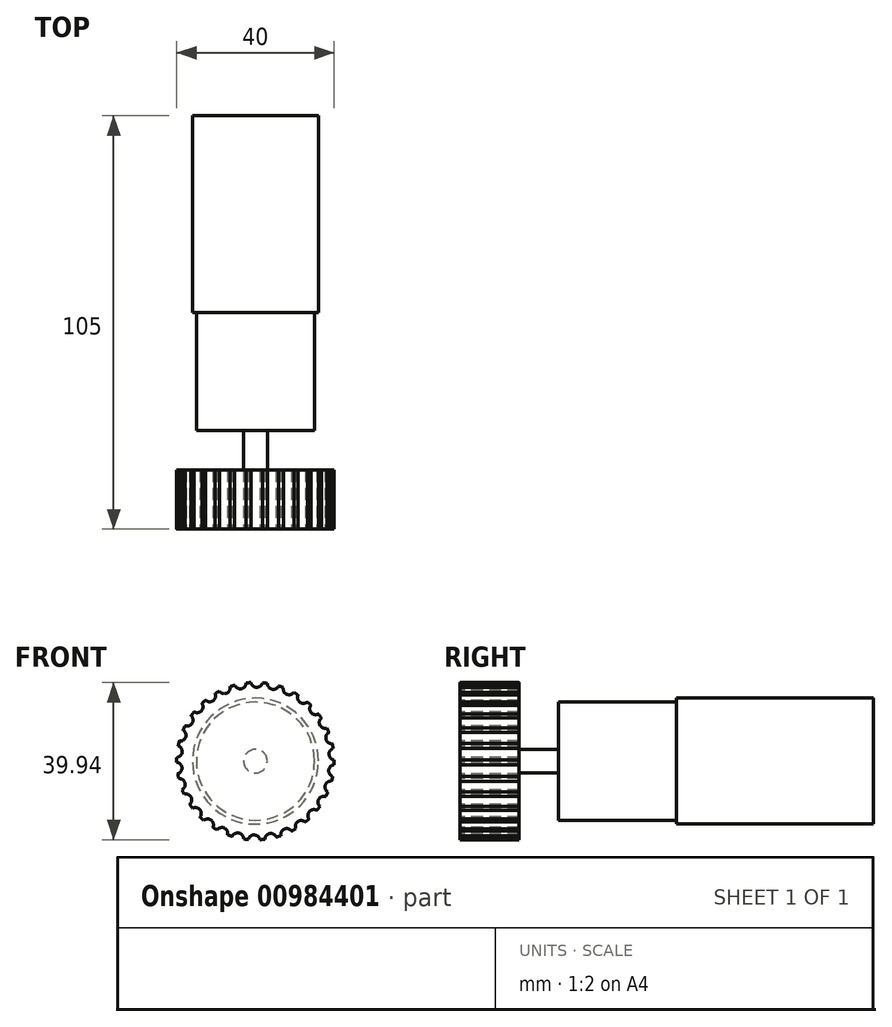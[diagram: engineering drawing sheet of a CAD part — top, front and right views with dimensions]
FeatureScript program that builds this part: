
annotation { "Feature Type Name" : "Feature", "Feature Type Description" : "" }
export const myFeature = defineFeature(function(context is Context, id is Id, definition is map)
    precondition{}
    {
        {
            var Q0;
            Q0=qCreatedBy(makeId("Front.planeOp"),FACE);
            var sketch = newSketch(context, id + "F0", { "sketchPlane" : qUnion([Q0])});
            skCircle(sketch, "E0", {"center": v(0, 0) * mm, "radius": 20 * mm});
            skCircle(sketch, "E1", {"center": v(0, 0) * mm, "radius": 3 * mm});
            skSolve(sketch);
        }
        {
            var Q0;
            Q0=makeQuery(id+"F0.imprint","IMPRINT",FACE,{"disambiguationData":[TD([[makeQuery(id+"F0.imprint","IMPRINT",EDGE,{"derivedFrom":sQuery(id+"F0.wireOp",EDGE,"E0")}),1.0]])]});
            extrude(context, id + "F1", {"entities" : qUnion([Q0]), "depth" : 15 * mm, "offsetDistance" : 25 * mm});
        }
        {
            var Q0;
            Q0=makeQuery(id+"F1.opExtrude","CAP_FACE",FACE,{"disambiguationData":[OSD([sQuery(id+"F0.wireOp",EDGE,"E0"),sQuery(id+"F0.wireOp",EDGE,"E1")])],"isStart":false});
            var sketch = newSketch(context, id + "F2", { "sketchPlane" : qUnion([Q0])});
            skCircle(sketch, "E2", {"center": v(20.17, 1.78) * mm, "radius": 1.5 * mm});
            skSolve(sketch);
        }
        {
            var Q0;
            Q0 = qSketchRegion(id + "F2", true);
            var Q1;
            Q1=sQuery(id+"F2.wireOp",EDGE,"E2");
            var Q2;
            Q2=makeQuery(id+"F1.opExtrude","CAP_FACE",FACE,{"disambiguationData":[OSD([sQuery(id+"F0.wireOp",EDGE,"E0"),sQuery(id+"F0.wireOp",EDGE,"E1")])],"isStart":true});
            extrude(context, id + "F3", {"entities" : qUnion([Q0]), "surfaceEntities" : qUnion([Q1]), "endBound" : BoundingType.UP_TO_SURFACE, "oppositeDirection" : true, "depth" : 25 * mm, "endBoundEntityFace" : qUnion([Q2]), "offsetDistance" : 25 * mm});
        }
        {
            var Q0;
            Q0=makeQuery(id+"F3.opExtrude","SWEPT_BODY",BODY,{"disambiguationData":[OSD([sQuery(id+"F2.wireOp",EDGE,"E2")])]});
            var Q1;
            Q1=makeQuery(id+"F1.opExtrude","SWEPT_FACE",FACE,{"disambiguationData":[OSD([sQuery(id+"F0.wireOp",EDGE,"E1")])]});
            circularPattern(context, id + "F4", {"entities" : qUnion([Q0]), "axis" : qUnion([Q1]), "angle" : 360 * degree, "instanceCount" : 30, "equalSpace" : true});
        }
        {
            var Q0;
            Q0=makeQuery(id+"F4.opPattern","COPY",BODY,{"derivedFrom":makeQuery(id+"F3.opExtrude","SWEPT_BODY",BODY,{"disambiguationData":[OSD([sQuery(id+"F2.wireOp",EDGE,"E2")])]}),"instanceName":"15"});
            var Q1;
            Q1=makeQuery(id+"F4.opPattern","COPY",BODY,{"derivedFrom":makeQuery(id+"F3.opExtrude","SWEPT_BODY",BODY,{"disambiguationData":[OSD([sQuery(id+"F2.wireOp",EDGE,"E2")])]}),"instanceName":"16"});
            var Q2;
            Q2=makeQuery(id+"F4.opPattern","COPY",BODY,{"derivedFrom":makeQuery(id+"F3.opExtrude","SWEPT_BODY",BODY,{"disambiguationData":[OSD([sQuery(id+"F2.wireOp",EDGE,"E2")])]}),"instanceName":"17"});
            var Q3;
            Q3=makeQuery(id+"F4.opPattern","COPY",BODY,{"derivedFrom":makeQuery(id+"F3.opExtrude","SWEPT_BODY",BODY,{"disambiguationData":[OSD([sQuery(id+"F2.wireOp",EDGE,"E2")])]}),"instanceName":"18"});
            var Q4;
            Q4=makeQuery(id+"F4.opPattern","COPY",BODY,{"derivedFrom":makeQuery(id+"F3.opExtrude","SWEPT_BODY",BODY,{"disambiguationData":[OSD([sQuery(id+"F2.wireOp",EDGE,"E2")])]}),"instanceName":"19"});
            var Q5;
            Q5=makeQuery(id+"F4.opPattern","COPY",BODY,{"derivedFrom":makeQuery(id+"F3.opExtrude","SWEPT_BODY",BODY,{"disambiguationData":[OSD([sQuery(id+"F2.wireOp",EDGE,"E2")])]}),"instanceName":"20"});
            var Q6;
            Q6=makeQuery(id+"F4.opPattern","COPY",BODY,{"derivedFrom":makeQuery(id+"F3.opExtrude","SWEPT_BODY",BODY,{"disambiguationData":[OSD([sQuery(id+"F2.wireOp",EDGE,"E2")])]}),"instanceName":"21"});
            var Q7;
            Q7=makeQuery(id+"F4.opPattern","COPY",BODY,{"derivedFrom":makeQuery(id+"F3.opExtrude","SWEPT_BODY",BODY,{"disambiguationData":[OSD([sQuery(id+"F2.wireOp",EDGE,"E2")])]}),"instanceName":"23"});
            var Q8;
            Q8=makeQuery(id+"F4.opPattern","COPY",BODY,{"derivedFrom":makeQuery(id+"F3.opExtrude","SWEPT_BODY",BODY,{"disambiguationData":[OSD([sQuery(id+"F2.wireOp",EDGE,"E2")])]}),"instanceName":"25"});
            var Q9;
            Q9=makeQuery(id+"F4.opPattern","COPY",BODY,{"derivedFrom":makeQuery(id+"F3.opExtrude","SWEPT_BODY",BODY,{"disambiguationData":[OSD([sQuery(id+"F2.wireOp",EDGE,"E2")])]}),"instanceName":"22"});
            var Q10;
            Q10=makeQuery(id+"F4.opPattern","COPY",BODY,{"derivedFrom":makeQuery(id+"F3.opExtrude","SWEPT_BODY",BODY,{"disambiguationData":[OSD([sQuery(id+"F2.wireOp",EDGE,"E2")])]}),"instanceName":"24"});
            var Q11;
            Q11=makeQuery(id+"F4.opPattern","COPY",BODY,{"derivedFrom":makeQuery(id+"F3.opExtrude","SWEPT_BODY",BODY,{"disambiguationData":[OSD([sQuery(id+"F2.wireOp",EDGE,"E2")])]}),"instanceName":"26"});
            var Q12;
            Q12=makeQuery(id+"F4.opPattern","COPY",BODY,{"derivedFrom":makeQuery(id+"F3.opExtrude","SWEPT_BODY",BODY,{"disambiguationData":[OSD([sQuery(id+"F2.wireOp",EDGE,"E2")])]}),"instanceName":"27"});
            var Q13;
            Q13=makeQuery(id+"F4.opPattern","COPY",BODY,{"derivedFrom":makeQuery(id+"F3.opExtrude","SWEPT_BODY",BODY,{"disambiguationData":[OSD([sQuery(id+"F2.wireOp",EDGE,"E2")])]}),"instanceName":"28"});
            var Q14;
            Q14=makeQuery(id+"F4.opPattern","COPY",BODY,{"derivedFrom":makeQuery(id+"F3.opExtrude","SWEPT_BODY",BODY,{"disambiguationData":[OSD([sQuery(id+"F2.wireOp",EDGE,"E2")])]}),"instanceName":"29"});
            var Q15;
            Q15=makeQuery(id+"F3.opExtrude","SWEPT_BODY",BODY,{"disambiguationData":[OSD([sQuery(id+"F2.wireOp",EDGE,"E2")])]});
            var Q16;
            Q16=makeQuery(id+"F4.opPattern","COPY",BODY,{"derivedFrom":makeQuery(id+"F3.opExtrude","SWEPT_BODY",BODY,{"disambiguationData":[OSD([sQuery(id+"F2.wireOp",EDGE,"E2")])]}),"instanceName":"1"});
            var Q17;
            Q17=makeQuery(id+"F4.opPattern","COPY",BODY,{"derivedFrom":makeQuery(id+"F3.opExtrude","SWEPT_BODY",BODY,{"disambiguationData":[OSD([sQuery(id+"F2.wireOp",EDGE,"E2")])]}),"instanceName":"2"});
            var Q18;
            Q18=makeQuery(id+"F4.opPattern","COPY",BODY,{"derivedFrom":makeQuery(id+"F3.opExtrude","SWEPT_BODY",BODY,{"disambiguationData":[OSD([sQuery(id+"F2.wireOp",EDGE,"E2")])]}),"instanceName":"3"});
            var Q19;
            Q19=makeQuery(id+"F4.opPattern","COPY",BODY,{"derivedFrom":makeQuery(id+"F3.opExtrude","SWEPT_BODY",BODY,{"disambiguationData":[OSD([sQuery(id+"F2.wireOp",EDGE,"E2")])]}),"instanceName":"4"});
            var Q20;
            Q20=makeQuery(id+"F4.opPattern","COPY",BODY,{"derivedFrom":makeQuery(id+"F3.opExtrude","SWEPT_BODY",BODY,{"disambiguationData":[OSD([sQuery(id+"F2.wireOp",EDGE,"E2")])]}),"instanceName":"5"});
            var Q21;
            Q21=makeQuery(id+"F4.opPattern","COPY",BODY,{"derivedFrom":makeQuery(id+"F3.opExtrude","SWEPT_BODY",BODY,{"disambiguationData":[OSD([sQuery(id+"F2.wireOp",EDGE,"E2")])]}),"instanceName":"6"});
            var Q22;
            Q22=makeQuery(id+"F4.opPattern","COPY",BODY,{"derivedFrom":makeQuery(id+"F3.opExtrude","SWEPT_BODY",BODY,{"disambiguationData":[OSD([sQuery(id+"F2.wireOp",EDGE,"E2")])]}),"instanceName":"7"});
            var Q23;
            Q23=makeQuery(id+"F4.opPattern","COPY",BODY,{"derivedFrom":makeQuery(id+"F3.opExtrude","SWEPT_BODY",BODY,{"disambiguationData":[OSD([sQuery(id+"F2.wireOp",EDGE,"E2")])]}),"instanceName":"8"});
            var Q24;
            Q24=makeQuery(id+"F4.opPattern","COPY",BODY,{"derivedFrom":makeQuery(id+"F3.opExtrude","SWEPT_BODY",BODY,{"disambiguationData":[OSD([sQuery(id+"F2.wireOp",EDGE,"E2")])]}),"instanceName":"9"});
            var Q25;
            Q25=makeQuery(id+"F4.opPattern","COPY",BODY,{"derivedFrom":makeQuery(id+"F3.opExtrude","SWEPT_BODY",BODY,{"disambiguationData":[OSD([sQuery(id+"F2.wireOp",EDGE,"E2")])]}),"instanceName":"10"});
            var Q26;
            Q26=makeQuery(id+"F4.opPattern","COPY",BODY,{"derivedFrom":makeQuery(id+"F3.opExtrude","SWEPT_BODY",BODY,{"disambiguationData":[OSD([sQuery(id+"F2.wireOp",EDGE,"E2")])]}),"instanceName":"11"});
            var Q27;
            Q27=makeQuery(id+"F4.opPattern","COPY",BODY,{"derivedFrom":makeQuery(id+"F3.opExtrude","SWEPT_BODY",BODY,{"disambiguationData":[OSD([sQuery(id+"F2.wireOp",EDGE,"E2")])]}),"instanceName":"12"});
            var Q28;
            Q28=makeQuery(id+"F4.opPattern","COPY",BODY,{"derivedFrom":makeQuery(id+"F3.opExtrude","SWEPT_BODY",BODY,{"disambiguationData":[OSD([sQuery(id+"F2.wireOp",EDGE,"E2")])]}),"instanceName":"13"});
            var Q29;
            Q29=makeQuery(id+"F4.opPattern","COPY",BODY,{"derivedFrom":makeQuery(id+"F3.opExtrude","SWEPT_BODY",BODY,{"disambiguationData":[OSD([sQuery(id+"F2.wireOp",EDGE,"E2")])]}),"instanceName":"14"});
            var Q30;
            Q30=makeQuery(id+"F1.opExtrude","SWEPT_BODY",BODY,{"disambiguationData":[OSD([sQuery(id+"F0.wireOp",EDGE,"E0"),sQuery(id+"F0.wireOp",EDGE,"E1")])]});
            booleanBodies(context, id + "F5", {"operationType" : BooleanOperationType.SUBTRACTION, "tools" : qUnion([Q0, Q1, Q2, Q3, Q4, Q5, Q6, Q7, Q8, Q9, Q10, Q11, Q12, Q13, Q14, Q15, Q16, Q17, Q18, Q19, Q20, Q21, Q22, Q23, Q24, Q25, Q26, Q27, Q28, Q29]), "targets" : qUnion([Q30])});
        }
        {
            var Q0;
            Q0=qCreatedBy(makeId("Right.planeOp"),FACE);
            var sketch = newSketch(context, id + "F6", { "sketchPlane" : qUnion([Q0])});
            skLineSegment(sketch, "E3", {"start": v(-15, 0) * mm, "end": v(-15, 3) * mm});
            skLineSegment(sketch, "E4", {"start": v(-15, 3) * mm, "end": v(10, 3) * mm});
            skLineSegment(sketch, "E5", {"start": v(10, 3) * mm, "end": v(10, 15) * mm});
            skLineSegment(sketch, "E6", {"start": v(10, 15) * mm, "end": v(40, 15) * mm});
            skLineSegment(sketch, "E7", {"start": v(40, 15) * mm, "end": v(40, 16) * mm});
            skLineSegment(sketch, "E8", {"start": v(40, 16) * mm, "end": v(90, 16) * mm});
            skLineSegment(sketch, "E9", {"start": v(90, 16) * mm, "end": v(90, 0) * mm});
            skLineSegment(sketch, "E10", {"start": v(-15, 0) * mm, "end": v(90, 0) * mm});
            skSolve(sketch);
        }
        {
            var Q0;
            Q0 = qSketchRegion(id + "F6", true);
            var Q1;
            Q1=sQuery(id+"F6.wireOp",EDGE,"E10");
            revolve(context, id + "F7", {"operationType" : NewBodyOperationType.ADD, "surfaceOperationType" : NewSurfaceOperationType.NEW, "entities" : qUnion([Q0]), "axis" : qUnion([Q1]), "revolveType" : RevolveType.FULL});
        }
    });
